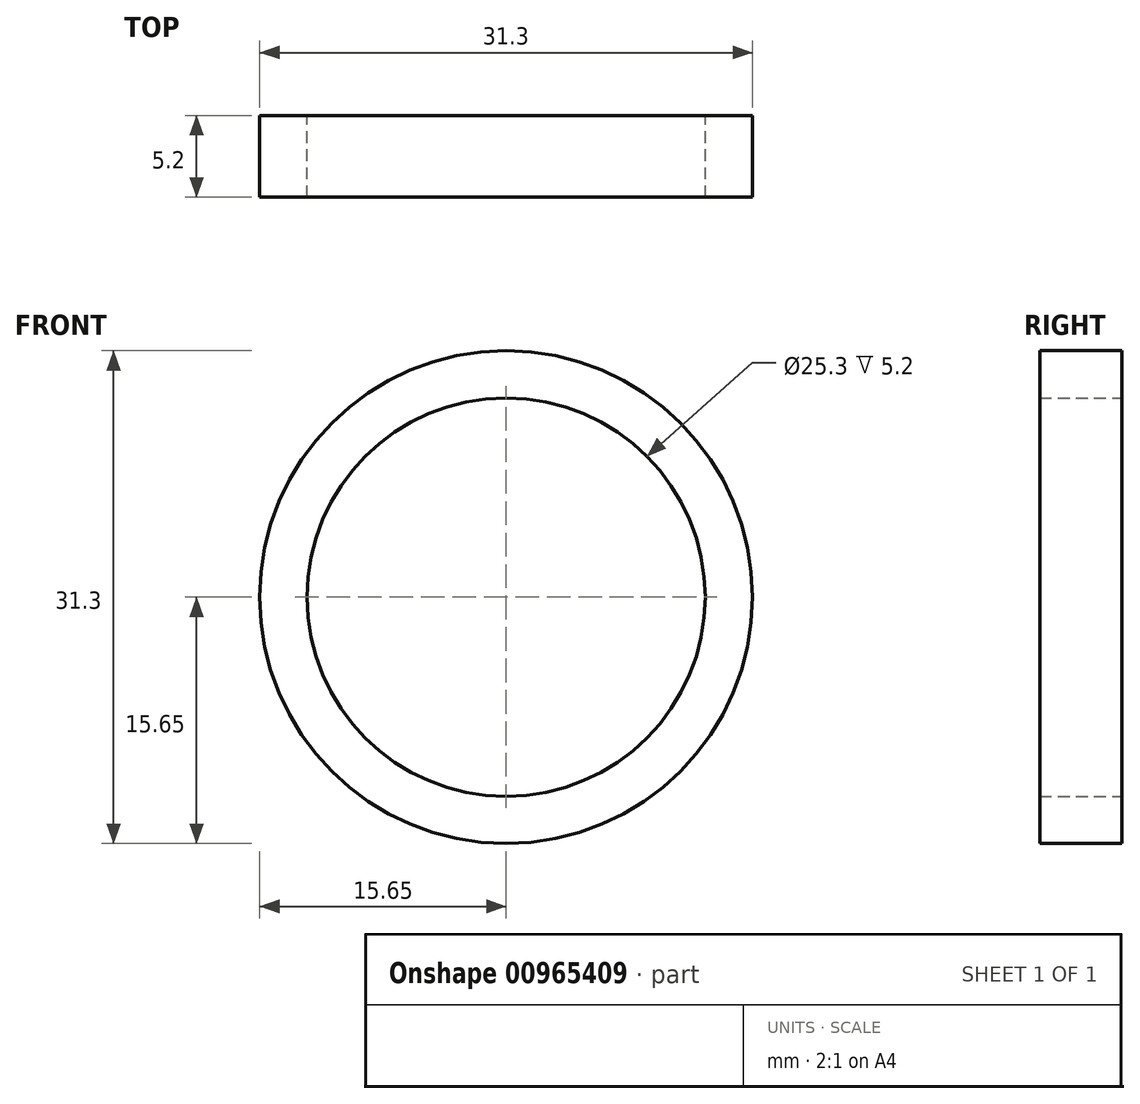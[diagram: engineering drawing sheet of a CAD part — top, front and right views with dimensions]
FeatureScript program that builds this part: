
annotation { "Feature Type Name" : "Feature", "Feature Type Description" : "" }
export const myFeature = defineFeature(function(context is Context, id is Id, definition is map)
    precondition{}
    {
        {
            var Q0;
            Q0=qCreatedBy(makeId("Front.planeOp"),FACE);
            var sketch = newSketch(context, id + "F0", { "sketchPlane" : qUnion([Q0])});
            skCircle(sketch, "E0", {"center": v(0, 0) * mm, "radius": 12.65 * mm});
            skCircle(sketch, "E1.0", {"center": v(0, 0) * mm, "radius": 15.65 * mm});
            skSolve(sketch);
        }
        {
            var Q0;
            Q0=makeQuery(id+"F0.imprint","IMPRINT",FACE,{"disambiguationData":[TD([[makeQuery(id+"F0.imprint","IMPRINT",EDGE,{"derivedFrom":sQuery(id+"F0.wireOp",EDGE,"E0")}),-1.0]])]});
            extrude(context, id + "F1", {"entities" : qUnion([Q0]), "depth" : 5.2 * mm, "offsetDistance" : 25 * mm});
        }
    });
